# Revit family: Specialty_Equipment-Fiberglass_Planter-Planters_Unlimited-Tuscana Rectangular & Square
name_source: partatom
category: Specialty Equipment
units: mm (PartAtom-declared; Revit-internal decimal feet)

## family parameters
Always vertical = Yes
Cut with Voids When Loaded = No
Enable Cutting in Views = No
Maintain Annotation Orientation = No
OmniClass Number = 23.40.05.21.17
OmniClass Title = Planters
Part Type = Normal
Room Calculation Point = No
Round Connector Dimension = Use Diameter
Shared = No
Work Plane-Based = No

## types (420) — shared parameters
Assembly Code = G2050600
CD_Divider Thickness = 0.4"
CD_Finish = Plastic-Fiberglass-Carlsbad-Semi_Gloss-Charcoal
CD_Microsite = https://www.caddetails.com
CD_OD = 0.4"
CD_Pad Size = 3.0"
CD_Pad Spacing = 5.0"
CD_Product Page URL = https://www.plantersunlimited.com
CD_Specification = https://www.plantersunlimited.com
Default Elevation = 0.0"
Manufacturer = Planters Unlimited
Model = Tuscana Series Planter
URL = https://www.plantersunlimited.com

## per-type parameters (varying)
| type | CD_Divider | CD_Height | CD_Length | CD_Width | Description | Type Comments |
| 30"L x 18"W x 18"H | No | 18.0" | 30.0" | 18.0" | Tuscana Rectangular Planter | Rectangular Planter |
| 30"L x 18"W x 24"H | No | 24.0" | 30.0" | 18.0" | Tuscana Rectangular Planter | Rectangular Planter |
| 30"L x 18"W x 30"H | No | 30.0" | 30.0" | 18.0" | Tuscana Rectangular Planter | Rectangular Planter |
| 30"L x 18"W x 36"H | No | 36.0" | 30.0" | 18.0" | Tuscana Rectangular Planter | Rectangular Planter |
| 30"L x 18"W x 42"H | No | 42.0" | 30.0" | 18.0" | Tuscana Rectangular Planter | Rectangular Planter |
| 30"L x 18"W x 48"H | No | 48.0" | 30.0" | 18.0" | Tuscana Rectangular Planter | Rectangular Planter |
| 30"L x 24"W x 18"H | No | 18.0" | 30.0" | 24.0" | Tuscana Rectangular Planter | Rectangular Planter |
| 30"L x 24"W x 24"H | No | 24.0" | 30.0" | 24.0" | Tuscana Rectangular Planter | Rectangular Planter |
| 30"L x 24"W x 30"H | No | 30.0" | 30.0" | 24.0" | Tuscana Rectangular Planter | Rectangular Planter |
| 30"L x 24"W x 36"H | No | 36.0" | 30.0" | 24.0" | Tuscana Rectangular Planter | Rectangular Planter |
| 30"L x 24"W x 42"H | No | 42.0" | 30.0" | 24.0" | Tuscana Rectangular Planter | Rectangular Planter |
| 30"L x 24"W x 48"H | No | 48.0" | 30.0" | 24.0" | Tuscana Rectangular Planter | Rectangular Planter |
| 30"L x 30"W x 18"H | No | 18.0" | 30.0" | 30.0" | Tuscana Square Planter | Square Planter |
| 30"L x 30"W x 24"H | No | 24.0" | 30.0" | 30.0" | Tuscana Square Planter | Square Planter |
| 30"L x 30"W x 30"H | No | 30.0" | 30.0" | 30.0" | Tuscana Square Planter | Square Planter |
| 30"L x 30"W x 36"H | No | 36.0" | 30.0" | 30.0" | Tuscana Square Planter | Square Planter |
| 30"L x 30"W x 42"H | No | 42.0" | 30.0" | 30.0" | Tuscana Square Planter | Square Planter |
| 30"L x 30"W x 48"H | No | 48.0" | 30.0" | 30.0" | Tuscana Square Planter | Square Planter |
| 30"L x 36"W x 18"H | No | 18.0" | 30.0" | 36.0" | Tuscana Rectangular Planter | Rectangular Planter |
| 30"L x 36"W x 24"H | No | 24.0" | 30.0" | 36.0" | Tuscana Rectangular Planter | Rectangular Planter |
| 30"L x 36"W x 30"H | No | 30.0" | 30.0" | 36.0" | Tuscana Rectangular Planter | Rectangular Planter |
| 30"L x 36"W x 36"H | No | 36.0" | 30.0" | 36.0" | Tuscana Rectangular Planter | Rectangular Planter |
| 30"L x 36"W x 42"H | No | 42.0" | 30.0" | 36.0" | Tuscana Rectangular Planter | Rectangular Planter |
| 30"L x 36"W x 48"H | No | 48.0" | 30.0" | 36.0" | Tuscana Rectangular Planter | Rectangular Planter |
| 30"L x 42"W x 18"H | No | 18.0" | 30.0" | 42.0" | Tuscana Rectangular Planter | Rectangular Planter |
| 30"L x 42"W x 24"H | No | 24.0" | 30.0" | 42.0" | Tuscana Rectangular Planter | Rectangular Planter |
| 30"L x 42"W x 30"H | No | 30.0" | 30.0" | 42.0" | Tuscana Rectangular Planter | Rectangular Planter |
| 30"L x 42"W x 36"H | No | 36.0" | 30.0" | 42.0" | Tuscana Rectangular Planter | Rectangular Planter |
| 30"L x 42"W x 42"H | No | 42.0" | 30.0" | 42.0" | Tuscana Rectangular Planter | Rectangular Planter |
| 30"L x 42"W x 48"H | No | 48.0" | 30.0" | 42.0" | Tuscana Rectangular Planter | Rectangular Planter |
| 36"L x 18"W x 18"H | No | 18.0" | 36.0" | 18.0" | Tuscana Rectangular Planter | Rectangular Planter |
| 36"L x 18"W x 24"H | No | 24.0" | 36.0" | 18.0" | Tuscana Rectangular Planter | Rectangular Planter |
| 36"L x 18"W x 30"H | No | 30.0" | 36.0" | 18.0" | Tuscana Rectangular Planter | Rectangular Planter |
| 36"L x 18"W x 36"H | No | 36.0" | 36.0" | 18.0" | Tuscana Rectangular Planter | Rectangular Planter |
| 36"L x 18"W x 42"H | No | 42.0" | 36.0" | 18.0" | Tuscana Rectangular Planter | Rectangular Planter |
| 36"L x 18"W x 48"H | No | 48.0" | 36.0" | 18.0" | Tuscana Rectangular Planter | Rectangular Planter |
| 36"L x 24"W x 18"H | No | 18.0" | 36.0" | 24.0" | Tuscana Rectangular Planter | Rectangular Planter |
| 36"L x 24"W x 24"H | No | 24.0" | 36.0" | 24.0" | Tuscana Rectangular Planter | Rectangular Planter |
| 36"L x 24"W x 30"H | No | 30.0" | 36.0" | 24.0" | Tuscana Rectangular Planter | Rectangular Planter |
| 36"L x 24"W x 36"H | No | 36.0" | 36.0" | 24.0" | Tuscana Rectangular Planter | Rectangular Planter |
| 36"L x 24"W x 42"H | No | 42.0" | 36.0" | 24.0" | Tuscana Rectangular Planter | Rectangular Planter |
| 36"L x 24"W x 48"H | No | 48.0" | 36.0" | 24.0" | Tuscana Rectangular Planter | Rectangular Planter |
| 36"L x 30"W x 18"H | No | 18.0" | 36.0" | 30.0" | Tuscana Rectangular Planter | Rectangular Planter |
| 36"L x 30"W x 24"H | No | 24.0" | 36.0" | 30.0" | Tuscana Rectangular Planter | Rectangular Planter |
| 36"L x 30"W x 30"H | No | 30.0" | 36.0" | 30.0" | Tuscana Rectangular Planter | Rectangular Planter |
| 36"L x 30"W x 36"H | No | 36.0" | 36.0" | 30.0" | Tuscana Rectangular Planter | Rectangular Planter |
| 36"L x 30"W x 42"H | No | 42.0" | 36.0" | 30.0" | Tuscana Rectangular Planter | Rectangular Planter |
| 36"L x 30"W x 48"H | No | 48.0" | 36.0" | 30.0" | Tuscana Rectangular Planter | Rectangular Planter |
| 36"L x 36"W x 18"H | No | 18.0" | 36.0" | 36.0" | Tuscana Square Planter | Square Planter |
| 36"L x 36"W x 24"H | No | 24.0" | 36.0" | 36.0" | Tuscana Square Planter | Square Planter |
| 36"L x 36"W x 30"H | No | 30.0" | 36.0" | 36.0" | Tuscana Square Planter | Square Planter |
| 36"L x 36"W x 36"H | No | 36.0" | 36.0" | 36.0" | Tuscana Square Planter | Square Planter |
| 36"L x 36"W x 42"H | No | 42.0" | 36.0" | 36.0" | Tuscana Square Planter | Square Planter |
| 36"L x 36"W x 48"H | No | 48.0" | 36.0" | 36.0" | Tuscana Square Planter | Square Planter |
| 36"L x 42"W x 18"H | No | 18.0" | 36.0" | 42.0" | Tuscana Rectangular Planter | Rectangular Planter |
| 36"L x 42"W x 24"H | No | 24.0" | 36.0" | 42.0" | Tuscana Rectangular Planter | Rectangular Planter |
| 36"L x 42"W x 30"H | No | 30.0" | 36.0" | 42.0" | Tuscana Rectangular Planter | Rectangular Planter |
| 36"L x 42"W x 36"H | No | 36.0" | 36.0" | 42.0" | Tuscana Rectangular Planter | Rectangular Planter |
| 36"L x 42"W x 42"H | No | 42.0" | 36.0" | 42.0" | Tuscana Rectangular Planter | Rectangular Planter |
| 36"L x 42"W x 48"H | No | 48.0" | 36.0" | 42.0" | Tuscana Rectangular Planter | Rectangular Planter |
| 42"L x 18"W x 18"H | No | 18.0" | 42.0" | 18.0" | Tuscana Rectangular Planter | Rectangular Planter |
| 42"L x 18"W x 24"H | No | 24.0" | 42.0" | 18.0" | Tuscana Rectangular Planter | Rectangular Planter |
| 42"L x 18"W x 30"H | No | 30.0" | 42.0" | 18.0" | Tuscana Rectangular Planter | Rectangular Planter |
| 42"L x 18"W x 36"H | No | 36.0" | 42.0" | 18.0" | Tuscana Rectangular Planter | Rectangular Planter |
| 42"L x 18"W x 42"H | No | 42.0" | 42.0" | 18.0" | Tuscana Rectangular Planter | Rectangular Planter |
| 42"L x 18"W x 48"H | No | 48.0" | 42.0" | 18.0" | Tuscana Rectangular Planter | Rectangular Planter |
| 42"L x 24"W x 18"H | No | 18.0" | 42.0" | 24.0" | Tuscana Rectangular Planter | Rectangular Planter |
| 42"L x 24"W x 24"H | No | 24.0" | 42.0" | 24.0" | Tuscana Rectangular Planter | Rectangular Planter |
| 42"L x 24"W x 30"H | No | 30.0" | 42.0" | 24.0" | Tuscana Rectangular Planter | Rectangular Planter |
| 42"L x 24"W x 36"H | No | 36.0" | 42.0" | 24.0" | Tuscana Rectangular Planter | Rectangular Planter |
| 42"L x 24"W x 42"H | No | 42.0" | 42.0" | 24.0" | Tuscana Rectangular Planter | Rectangular Planter |
| 42"L x 24"W x 48"H | No | 48.0" | 42.0" | 24.0" | Tuscana Rectangular Planter | Rectangular Planter |
| 42"L x 30"W x 18"H | No | 18.0" | 42.0" | 30.0" | Tuscana Rectangular Planter | Rectangular Planter |
| 42"L x 30"W x 24"H | No | 24.0" | 42.0" | 30.0" | Tuscana Rectangular Planter | Rectangular Planter |
| 42"L x 30"W x 30"H | No | 30.0" | 42.0" | 30.0" | Tuscana Rectangular Planter | Rectangular Planter |
| 42"L x 30"W x 36"H | No | 36.0" | 42.0" | 30.0" | Tuscana Rectangular Planter | Rectangular Planter |
| 42"L x 30"W x 42"H | No | 42.0" | 42.0" | 30.0" | Tuscana Rectangular Planter | Rectangular Planter |
| 42"L x 30"W x 48"H | No | 48.0" | 42.0" | 30.0" | Tuscana Rectangular Planter | Rectangular Planter |
| 42"L x 36"W x 18"H | No | 18.0" | 42.0" | 36.0" | Tuscana Rectangular Planter | Rectangular Planter |
| 42"L x 36"W x 24"H | No | 24.0" | 42.0" | 36.0" | Tuscana Rectangular Planter | Rectangular Planter |
| 42"L x 36"W x 30"H | No | 30.0" | 42.0" | 36.0" | Tuscana Rectangular Planter | Rectangular Planter |
| 42"L x 36"W x 36"H | No | 36.0" | 42.0" | 36.0" | Tuscana Rectangular Planter | Rectangular Planter |
| 42"L x 36"W x 42"H | No | 42.0" | 42.0" | 36.0" | Tuscana Rectangular Planter | Rectangular Planter |
| 42"L x 36"W x 48"H | No | 48.0" | 42.0" | 36.0" | Tuscana Rectangular Planter | Rectangular Planter |
| 42"L x 42"W x 18"H | No | 18.0" | 42.0" | 42.0" | Tuscana Square Planter | Square Planter |
| 42"L x 42"W x 24"H | No | 24.0" | 42.0" | 42.0" | Tuscana Square Planter | Square Planter |
| 42"L x 42"W x 30"H | No | 30.0" | 42.0" | 42.0" | Tuscana Square Planter | Square Planter |
| 42"L x 42"W x 36"H | No | 36.0" | 42.0" | 42.0" | Tuscana Square Planter | Square Planter |
| 42"L x 42"W x 42"H | No | 42.0" | 42.0" | 42.0" | Tuscana Square Planter | Square Planter |
| 42"L x 42"W x 48"H | No | 48.0" | 42.0" | 42.0" | Tuscana Square Planter | Square Planter |
| 48"L x 18"W x 18"H | No | 18.0" | 48.0" | 18.0" | Tuscana Rectangular Planter | Rectangular Planter |
| 48"L x 18"W x 24"H | No | 24.0" | 48.0" | 18.0" | Tuscana Rectangular Planter | Rectangular Planter |
| 48"L x 18"W x 30"H | No | 30.0" | 48.0" | 18.0" | Tuscana Rectangular Planter | Rectangular Planter |
| 48"L x 18"W x 36"H | No | 36.0" | 48.0" | 18.0" | Tuscana Rectangular Planter | Rectangular Planter |
| 48"L x 18"W x 42"H | No | 42.0" | 48.0" | 18.0" | Tuscana Rectangular Planter | Rectangular Planter |
| 48"L x 18"W x 48"H | No | 48.0" | 48.0" | 18.0" | Tuscana Rectangular Planter | Rectangular Planter |
| 48"L x 24"W x 18"H | No | 18.0" | 48.0" | 24.0" | Tuscana Rectangular Planter | Rectangular Planter |
| 48"L x 24"W x 24"H | No | 24.0" | 48.0" | 24.0" | Tuscana Rectangular Planter | Rectangular Planter |
| 48"L x 24"W x 30"H | No | 30.0" | 48.0" | 24.0" | Tuscana Rectangular Planter | Rectangular Planter |
| 48"L x 24"W x 36"H | No | 36.0" | 48.0" | 24.0" | Tuscana Rectangular Planter | Rectangular Planter |
| 48"L x 24"W x 42"H | No | 42.0" | 48.0" | 24.0" | Tuscana Rectangular Planter | Rectangular Planter |
| 48"L x 24"W x 48"H | No | 48.0" | 48.0" | 24.0" | Tuscana Rectangular Planter | Rectangular Planter |
| 48"L x 30"W x 18"H | No | 18.0" | 48.0" | 30.0" | Tuscana Rectangular Planter | Rectangular Planter |
| 48"L x 30"W x 24"H | No | 24.0" | 48.0" | 30.0" | Tuscana Rectangular Planter | Rectangular Planter |
| 48"L x 30"W x 30"H | No | 30.0" | 48.0" | 30.0" | Tuscana Rectangular Planter | Rectangular Planter |
| 48"L x 30"W x 36"H | No | 36.0" | 48.0" | 30.0" | Tuscana Rectangular Planter | Rectangular Planter |
| 48"L x 30"W x 42"H | No | 42.0" | 48.0" | 30.0" | Tuscana Rectangular Planter | Rectangular Planter |
| 48"L x 30"W x 48"H | No | 48.0" | 48.0" | 30.0" | Tuscana Rectangular Planter | Rectangular Planter |
| 48"L x 36"W x 18"H | No | 18.0" | 48.0" | 36.0" | Tuscana Rectangular Planter | Rectangular Planter |
| 48"L x 36"W x 24"H | No | 24.0" | 48.0" | 36.0" | Tuscana Rectangular Planter | Rectangular Planter |
| 48"L x 36"W x 30"H | No | 30.0" | 48.0" | 36.0" | Tuscana Rectangular Planter | Rectangular Planter |
| 48"L x 36"W x 36"H | No | 36.0" | 48.0" | 36.0" | Tuscana Rectangular Planter | Rectangular Planter |
| 48"L x 36"W x 42"H | No | 42.0" | 48.0" | 36.0" | Tuscana Rectangular Planter | Rectangular Planter |
| 48"L x 36"W x 48"H | No | 48.0" | 48.0" | 36.0" | Tuscana Rectangular Planter | Rectangular Planter |
| 48"L x 42"W x 18"H | No | 18.0" | 48.0" | 42.0" | Tuscana Rectangular Planter | Rectangular Planter |
| 48"L x 42"W x 24"H | No | 24.0" | 48.0" | 42.0" | Tuscana Rectangular Planter | Rectangular Planter |
| 48"L x 42"W x 30"H | No | 30.0" | 48.0" | 42.0" | Tuscana Rectangular Planter | Rectangular Planter |
| 48"L x 42"W x 36"H | No | 36.0" | 48.0" | 42.0" | Tuscana Rectangular Planter | Rectangular Planter |
| 48"L x 42"W x 42"H | No | 42.0" | 48.0" | 42.0" | Tuscana Rectangular Planter | Rectangular Planter |
| 48"L x 42"W x 48"H | No | 48.0" | 48.0" | 42.0" | Tuscana Rectangular Planter | Rectangular Planter |
| 54"L x 18"W x 18"H | Yes | 18.0" | 54.0" | 18.0" | Tuscana Rectangular Planter | Rectangular Planter |
| 54"L x 18"W x 24"H | Yes | 24.0" | 54.0" | 18.0" | Tuscana Rectangular Planter | Rectangular Planter |
| 54"L x 18"W x 30"H | Yes | 30.0" | 54.0" | 18.0" | Tuscana Rectangular Planter | Rectangular Planter |
| 54"L x 18"W x 36"H | Yes | 36.0" | 54.0" | 18.0" | Tuscana Rectangular Planter | Rectangular Planter |
| 54"L x 18"W x 42"H | Yes | 42.0" | 54.0" | 18.0" | Tuscana Rectangular Planter | Rectangular Planter |
| 54"L x 18"W x 48"H | Yes | 48.0" | 54.0" | 18.0" | Tuscana Rectangular Planter | Rectangular Planter |
| 54"L x 24"W x 18"H | Yes | 18.0" | 54.0" | 24.0" | Tuscana Rectangular Planter | Rectangular Planter |
| 54"L x 24"W x 24"H | Yes | 24.0" | 54.0" | 24.0" | Tuscana Rectangular Planter | Rectangular Planter |
| 54"L x 24"W x 30"H | Yes | 30.0" | 54.0" | 24.0" | Tuscana Rectangular Planter | Rectangular Planter |
| 54"L x 24"W x 36"H | Yes | 36.0" | 54.0" | 24.0" | Tuscana Rectangular Planter | Rectangular Planter |
| 54"L x 24"W x 42"H | Yes | 42.0" | 54.0" | 24.0" | Tuscana Rectangular Planter | Rectangular Planter |
| 54"L x 24"W x 48"H | Yes | 48.0" | 54.0" | 24.0" | Tuscana Rectangular Planter | Rectangular Planter |
| 54"L x 30"W x 18"H | Yes | 18.0" | 54.0" | 30.0" | Tuscana Rectangular Planter | Rectangular Planter |
| 54"L x 30"W x 24"H | Yes | 24.0" | 54.0" | 30.0" | Tuscana Rectangular Planter | Rectangular Planter |
| 54"L x 30"W x 30"H | Yes | 30.0" | 54.0" | 30.0" | Tuscana Rectangular Planter | Rectangular Planter |
| 54"L x 30"W x 36"H | Yes | 36.0" | 54.0" | 30.0" | Tuscana Rectangular Planter | Rectangular Planter |
| 54"L x 30"W x 42"H | Yes | 42.0" | 54.0" | 30.0" | Tuscana Rectangular Planter | Rectangular Planter |
| 54"L x 30"W x 48"H | Yes | 48.0" | 54.0" | 30.0" | Tuscana Rectangular Planter | Rectangular Planter |
| 54"L x 36"W x 18"H | Yes | 18.0" | 54.0" | 36.0" | Tuscana Rectangular Planter | Rectangular Planter |
| 54"L x 36"W x 24"H | Yes | 24.0" | 54.0" | 36.0" | Tuscana Rectangular Planter | Rectangular Planter |
| 54"L x 36"W x 30"H | Yes | 30.0" | 54.0" | 36.0" | Tuscana Rectangular Planter | Rectangular Planter |
| 54"L x 36"W x 36"H | Yes | 36.0" | 54.0" | 36.0" | Tuscana Rectangular Planter | Rectangular Planter |
| 54"L x 36"W x 42"H | Yes | 42.0" | 54.0" | 36.0" | Tuscana Rectangular Planter | Rectangular Planter |
| 54"L x 36"W x 48"H | Yes | 48.0" | 54.0" | 36.0" | Tuscana Rectangular Planter | Rectangular Planter |
| 54"L x 42"W x 18"H | Yes | 18.0" | 54.0" | 42.0" | Tuscana Rectangular Planter | Rectangular Planter |
| 54"L x 42"W x 24"H | Yes | 24.0" | 54.0" | 42.0" | Tuscana Rectangular Planter | Rectangular Planter |
| 54"L x 42"W x 30"H | Yes | 30.0" | 54.0" | 42.0" | Tuscana Rectangular Planter | Rectangular Planter |
| 54"L x 42"W x 36"H | Yes | 36.0" | 54.0" | 42.0" | Tuscana Rectangular Planter | Rectangular Planter |
| 54"L x 42"W x 42"H | Yes | 42.0" | 54.0" | 42.0" | Tuscana Rectangular Planter | Rectangular Planter |
| 54"L x 42"W x 48"H | Yes | 48.0" | 54.0" | 42.0" | Tuscana Rectangular Planter | Rectangular Planter |
| 60"L x 18"W x 18"H | Yes | 18.0" | 60.0" | 18.0" | Tuscana Rectangular Planter | Rectangular Planter |
| 60"L x 18"W x 24"H | Yes | 24.0" | 60.0" | 18.0" | Tuscana Rectangular Planter | Rectangular Planter |
| 60"L x 18"W x 30"H | Yes | 30.0" | 60.0" | 18.0" | Tuscana Rectangular Planter | Rectangular Planter |
| 60"L x 18"W x 36"H | Yes | 36.0" | 60.0" | 18.0" | Tuscana Rectangular Planter | Rectangular Planter |
| 60"L x 18"W x 42"H | Yes | 42.0" | 60.0" | 18.0" | Tuscana Rectangular Planter | Rectangular Planter |
| 60"L x 18"W x 48"H | Yes | 48.0" | 60.0" | 18.0" | Tuscana Rectangular Planter | Rectangular Planter |
| 60"L x 24"W x 18"H | Yes | 18.0" | 60.0" | 24.0" | Tuscana Rectangular Planter | Rectangular Planter |
| 60"L x 24"W x 24"H | Yes | 24.0" | 60.0" | 24.0" | Tuscana Rectangular Planter | Rectangular Planter |
| 60"L x 24"W x 30"H | Yes | 30.0" | 60.0" | 24.0" | Tuscana Rectangular Planter | Rectangular Planter |
| 60"L x 24"W x 36"H | Yes | 36.0" | 60.0" | 24.0" | Tuscana Rectangular Planter | Rectangular Planter |
| 60"L x 24"W x 42"H | Yes | 42.0" | 60.0" | 24.0" | Tuscana Rectangular Planter | Rectangular Planter |
| 60"L x 24"W x 48"H | Yes | 48.0" | 60.0" | 24.0" | Tuscana Rectangular Planter | Rectangular Planter |
| 60"L x 30"W x 18"H | Yes | 18.0" | 60.0" | 30.0" | Tuscana Rectangular Planter | Rectangular Planter |
| 60"L x 30"W x 24"H | Yes | 24.0" | 60.0" | 30.0" | Tuscana Rectangular Planter | Rectangular Planter |
| 60"L x 30"W x 30"H | Yes | 30.0" | 60.0" | 30.0" | Tuscana Rectangular Planter | Rectangular Planter |
| 60"L x 30"W x 36"H | Yes | 36.0" | 60.0" | 30.0" | Tuscana Rectangular Planter | Rectangular Planter |
| 60"L x 30"W x 42"H | Yes | 42.0" | 60.0" | 30.0" | Tuscana Rectangular Planter | Rectangular Planter |
| 60"L x 30"W x 48"H | Yes | 48.0" | 60.0" | 30.0" | Tuscana Rectangular Planter | Rectangular Planter |
| 60"L x 36"W x 18"H | Yes | 18.0" | 60.0" | 36.0" | Tuscana Rectangular Planter | Rectangular Planter |
| 60"L x 36"W x 24"H | Yes | 24.0" | 60.0" | 36.0" | Tuscana Rectangular Planter | Rectangular Planter |
| 60"L x 36"W x 30"H | Yes | 30.0" | 60.0" | 36.0" | Tuscana Rectangular Planter | Rectangular Planter |
| 60"L x 36"W x 36"H | Yes | 36.0" | 60.0" | 36.0" | Tuscana Rectangular Planter | Rectangular Planter |
| 60"L x 36"W x 42"H | Yes | 42.0" | 60.0" | 36.0" | Tuscana Rectangular Planter | Rectangular Planter |
| 60"L x 36"W x 48"H | Yes | 48.0" | 60.0" | 36.0" | Tuscana Rectangular Planter | Rectangular Planter |
| 60"L x 42"W x 18"H | Yes | 18.0" | 60.0" | 42.0" | Tuscana Rectangular Planter | Rectangular Planter |
| 60"L x 42"W x 24"H | Yes | 24.0" | 60.0" | 42.0" | Tuscana Rectangular Planter | Rectangular Planter |
| 60"L x 42"W x 30"H | Yes | 30.0" | 60.0" | 42.0" | Tuscana Rectangular Planter | Rectangular Planter |
| 60"L x 42"W x 36"H | Yes | 36.0" | 60.0" | 42.0" | Tuscana Rectangular Planter | Rectangular Planter |
| 60"L x 42"W x 42"H | Yes | 42.0" | 60.0" | 42.0" | Tuscana Rectangular Planter | Rectangular Planter |
| 60"L x 42"W x 48"H | Yes | 48.0" | 60.0" | 42.0" | Tuscana Rectangular Planter | Rectangular Planter |
| 66"L x 18"W x 18"H | Yes | 18.0" | 66.0" | 18.0" | Tuscana Rectangular Planter | Rectangular Planter |
| 66"L x 18"W x 24"H | Yes | 24.0" | 66.0" | 18.0" | Tuscana Rectangular Planter | Rectangular Planter |
| 66"L x 18"W x 30"H | Yes | 30.0" | 66.0" | 18.0" | Tuscana Rectangular Planter | Rectangular Planter |
| 66"L x 18"W x 36"H | Yes | 36.0" | 66.0" | 18.0" | Tuscana Rectangular Planter | Rectangular Planter |
| 66"L x 18"W x 42"H | Yes | 42.0" | 66.0" | 18.0" | Tuscana Rectangular Planter | Rectangular Planter |
| 66"L x 18"W x 48"H | Yes | 48.0" | 66.0" | 18.0" | Tuscana Rectangular Planter | Rectangular Planter |
| 66"L x 24"W x 18"H | Yes | 18.0" | 66.0" | 24.0" | Tuscana Rectangular Planter | Rectangular Planter |
| 66"L x 24"W x 24"H | Yes | 24.0" | 66.0" | 24.0" | Tuscana Rectangular Planter | Rectangular Planter |
| 66"L x 24"W x 30"H | Yes | 30.0" | 66.0" | 24.0" | Tuscana Rectangular Planter | Rectangular Planter |
| 66"L x 24"W x 36"H | Yes | 36.0" | 66.0" | 24.0" | Tuscana Rectangular Planter | Rectangular Planter |
| 66"L x 24"W x 42"H | Yes | 42.0" | 66.0" | 24.0" | Tuscana Rectangular Planter | Rectangular Planter |
| 66"L x 24"W x 48"H | Yes | 48.0" | 66.0" | 24.0" | Tuscana Rectangular Planter | Rectangular Planter |
| 66"L x 30"W x 18"H | Yes | 18.0" | 66.0" | 30.0" | Tuscana Rectangular Planter | Rectangular Planter |
| 66"L x 30"W x 24"H | Yes | 24.0" | 66.0" | 30.0" | Tuscana Rectangular Planter | Rectangular Planter |
| 66"L x 30"W x 30"H | Yes | 30.0" | 66.0" | 30.0" | Tuscana Rectangular Planter | Rectangular Planter |
| 66"L x 30"W x 36"H | Yes | 36.0" | 66.0" | 30.0" | Tuscana Rectangular Planter | Rectangular Planter |
| 66"L x 30"W x 42"H | Yes | 42.0" | 66.0" | 30.0" | Tuscana Rectangular Planter | Rectangular Planter |
| 66"L x 30"W x 48"H | Yes | 48.0" | 66.0" | 30.0" | Tuscana Rectangular Planter | Rectangular Planter |
| 66"L x 36"W x 18"H | Yes | 18.0" | 66.0" | 36.0" | Tuscana Rectangular Planter | Rectangular Planter |
| 66"L x 36"W x 24"H | Yes | 24.0" | 66.0" | 36.0" | Tuscana Rectangular Planter | Rectangular Planter |
| 66"L x 36"W x 30"H | Yes | 30.0" | 66.0" | 36.0" | Tuscana Rectangular Planter | Rectangular Planter |
| 66"L x 36"W x 36"H | Yes | 36.0" | 66.0" | 36.0" | Tuscana Rectangular Planter | Rectangular Planter |
| 66"L x 36"W x 42"H | Yes | 42.0" | 66.0" | 36.0" | Tuscana Rectangular Planter | Rectangular Planter |
| 66"L x 36"W x 48"H | Yes | 48.0" | 66.0" | 36.0" | Tuscana Rectangular Planter | Rectangular Planter |
| 66"L x 42"W x 18"H | Yes | 18.0" | 66.0" | 42.0" | Tuscana Rectangular Planter | Rectangular Planter |
| 66"L x 42"W x 24"H | Yes | 24.0" | 66.0" | 42.0" | Tuscana Rectangular Planter | Rectangular Planter |
| 66"L x 42"W x 30"H | Yes | 30.0" | 66.0" | 42.0" | Tuscana Rectangular Planter | Rectangular Planter |
| 66"L x 42"W x 36"H | Yes | 36.0" | 66.0" | 42.0" | Tuscana Rectangular Planter | Rectangular Planter |
| 66"L x 42"W x 42"H | Yes | 42.0" | 66.0" | 42.0" | Tuscana Rectangular Planter | Rectangular Planter |
| 66"L x 42"W x 48"H | Yes | 48.0" | 66.0" | 42.0" | Tuscana Rectangular Planter | Rectangular Planter |
| 72"L x 18"W x 18"H | Yes | 18.0" | 72.0" | 18.0" | Tuscana Rectangular Planter | Rectangular Planter |
| 72"L x 18"W x 24"H | Yes | 24.0" | 72.0" | 18.0" | Tuscana Rectangular Planter | Rectangular Planter |
| 72"L x 18"W x 30"H | Yes | 30.0" | 72.0" | 18.0" | Tuscana Rectangular Planter | Rectangular Planter |
| 72"L x 18"W x 36"H | Yes | 36.0" | 72.0" | 18.0" | Tuscana Rectangular Planter | Rectangular Planter |
| 72"L x 18"W x 42"H | Yes | 42.0" | 72.0" | 18.0" | Tuscana Rectangular Planter | Rectangular Planter |
| 72"L x 18"W x 48"H | Yes | 48.0" | 72.0" | 18.0" | Tuscana Rectangular Planter | Rectangular Planter |
| 72"L x 24"W x 18"H | Yes | 18.0" | 72.0" | 24.0" | Tuscana Rectangular Planter | Rectangular Planter |
| 72"L x 24"W x 24"H | Yes | 24.0" | 72.0" | 24.0" | Tuscana Rectangular Planter | Rectangular Planter |
| 72"L x 24"W x 30"H | Yes | 30.0" | 72.0" | 24.0" | Tuscana Rectangular Planter | Rectangular Planter |
| 72"L x 24"W x 36"H | Yes | 36.0" | 72.0" | 24.0" | Tuscana Rectangular Planter | Rectangular Planter |
| 72"L x 24"W x 42"H | Yes | 42.0" | 72.0" | 24.0" | Tuscana Rectangular Planter | Rectangular Planter |
| 72"L x 24"W x 48"H | Yes | 48.0" | 72.0" | 24.0" | Tuscana Rectangular Planter | Rectangular Planter |
| 72"L x 30"W x 18"H | Yes | 18.0" | 72.0" | 30.0" | Tuscana Rectangular Planter | Rectangular Planter |
| 72"L x 30"W x 24"H | Yes | 24.0" | 72.0" | 30.0" | Tuscana Rectangular Planter | Rectangular Planter |
| 72"L x 30"W x 30"H | Yes | 30.0" | 72.0" | 30.0" | Tuscana Rectangular Planter | Rectangular Planter |
| 72"L x 30"W x 36"H | Yes | 36.0" | 72.0" | 30.0" | Tuscana Rectangular Planter | Rectangular Planter |
| 72"L x 30"W x 42"H | Yes | 42.0" | 72.0" | 30.0" | Tuscana Rectangular Planter | Rectangular Planter |
| 72"L x 30"W x 48"H | Yes | 48.0" | 72.0" | 30.0" | Tuscana Rectangular Planter | Rectangular Planter |
| 72"L x 36"W x 18"H | Yes | 18.0" | 72.0" | 36.0" | Tuscana Rectangular Planter | Rectangular Planter |
| 72"L x 36"W x 24"H | Yes | 24.0" | 72.0" | 36.0" | Tuscana Rectangular Planter | Rectangular Planter |
| 72"L x 36"W x 30"H | Yes | 30.0" | 72.0" | 36.0" | Tuscana Rectangular Planter | Rectangular Planter |
| 72"L x 36"W x 36"H | Yes | 36.0" | 72.0" | 36.0" | Tuscana Rectangular Planter | Rectangular Planter |
| 72"L x 36"W x 42"H | Yes | 42.0" | 72.0" | 36.0" | Tuscana Rectangular Planter | Rectangular Planter |
| 72"L x 36"W x 48"H | Yes | 48.0" | 72.0" | 36.0" | Tuscana Rectangular Planter | Rectangular Planter |
| 72"L x 42"W x 18"H | Yes | 18.0" | 72.0" | 42.0" | Tuscana Rectangular Planter | Rectangular Planter |
| 72"L x 42"W x 24"H | Yes | 24.0" | 72.0" | 42.0" | Tuscana Rectangular Planter | Rectangular Planter |
| 72"L x 42"W x 30"H | Yes | 30.0" | 72.0" | 42.0" | Tuscana Rectangular Planter | Rectangular Planter |
| 72"L x 42"W x 36"H | Yes | 36.0" | 72.0" | 42.0" | Tuscana Rectangular Planter | Rectangular Planter |
| 72"L x 42"W x 42"H | Yes | 42.0" | 72.0" | 42.0" | Tuscana Rectangular Planter | Rectangular Planter |
| 72"L x 42"W x 48"H | Yes | 48.0" | 72.0" | 42.0" | Tuscana Rectangular Planter | Rectangular Planter |
| 78"L x 18"W x 18"H | Yes | 18.0" | 78.0" | 18.0" | Tuscana Rectangular Planter | Rectangular Planter |
| 78"L x 18"W x 24"H | Yes | 24.0" | 78.0" | 18.0" | Tuscana Rectangular Planter | Rectangular Planter |
| 78"L x 18"W x 30"H | Yes | 30.0" | 78.0" | 18.0" | Tuscana Rectangular Planter | Rectangular Planter |
| 78"L x 18"W x 36"H | Yes | 36.0" | 78.0" | 18.0" | Tuscana Rectangular Planter | Rectangular Planter |
| 78"L x 18"W x 42"H | Yes | 42.0" | 78.0" | 18.0" | Tuscana Rectangular Planter | Rectangular Planter |
| 78"L x 18"W x 48"H | Yes | 48.0" | 78.0" | 18.0" | Tuscana Rectangular Planter | Rectangular Planter |
| 78"L x 24"W x 18"H | Yes | 18.0" | 78.0" | 24.0" | Tuscana Rectangular Planter | Rectangular Planter |
| 78"L x 24"W x 24"H | Yes | 24.0" | 78.0" | 24.0" | Tuscana Rectangular Planter | Rectangular Planter |
| 78"L x 24"W x 30"H | Yes | 30.0" | 78.0" | 24.0" | Tuscana Rectangular Planter | Rectangular Planter |
| 78"L x 24"W x 36"H | Yes | 36.0" | 78.0" | 24.0" | Tuscana Rectangular Planter | Rectangular Planter |
| 78"L x 24"W x 42"H | Yes | 42.0" | 78.0" | 24.0" | Tuscana Rectangular Planter | Rectangular Planter |
| 78"L x 24"W x 48"H | Yes | 48.0" | 78.0" | 24.0" | Tuscana Rectangular Planter | Rectangular Planter |
| 78"L x 30"W x 18"H | Yes | 18.0" | 78.0" | 30.0" | Tuscana Rectangular Planter | Rectangular Planter |
| 78"L x 30"W x 24"H | Yes | 24.0" | 78.0" | 30.0" | Tuscana Rectangular Planter | Rectangular Planter |
| 78"L x 30"W x 30"H | Yes | 30.0" | 78.0" | 30.0" | Tuscana Rectangular Planter | Rectangular Planter |
| 78"L x 30"W x 36"H | Yes | 36.0" | 78.0" | 30.0" | Tuscana Rectangular Planter | Rectangular Planter |
| 78"L x 30"W x 42"H | Yes | 42.0" | 78.0" | 30.0" | Tuscana Rectangular Planter | Rectangular Planter |
| 78"L x 30"W x 48"H | Yes | 48.0" | 78.0" | 30.0" | Tuscana Rectangular Planter | Rectangular Planter |
| 78"L x 36"W x 18"H | Yes | 18.0" | 78.0" | 36.0" | Tuscana Rectangular Planter | Rectangular Planter |
| 78"L x 36"W x 24"H | Yes | 24.0" | 78.0" | 36.0" | Tuscana Rectangular Planter | Rectangular Planter |
| 78"L x 36"W x 30"H | Yes | 30.0" | 78.0" | 36.0" | Tuscana Rectangular Planter | Rectangular Planter |
| 78"L x 36"W x 36"H | Yes | 36.0" | 78.0" | 36.0" | Tuscana Rectangular Planter | Rectangular Planter |
| 78"L x 36"W x 42"H | Yes | 42.0" | 78.0" | 36.0" | Tuscana Rectangular Planter | Rectangular Planter |
| 78"L x 36"W x 48"H | Yes | 48.0" | 78.0" | 36.0" | Tuscana Rectangular Planter | Rectangular Planter |
| 78"L x 42"W x 18"H | Yes | 18.0" | 78.0" | 42.0" | Tuscana Rectangular Planter | Rectangular Planter |
| 78"L x 42"W x 24"H | Yes | 24.0" | 78.0" | 42.0" | Tuscana Rectangular Planter | Rectangular Planter |
| 78"L x 42"W x 30"H | Yes | 30.0" | 78.0" | 42.0" | Tuscana Rectangular Planter | Rectangular Planter |
| 78"L x 42"W x 36"H | Yes | 36.0" | 78.0" | 42.0" | Tuscana Rectangular Planter | Rectangular Planter |
| 78"L x 42"W x 42"H | Yes | 42.0" | 78.0" | 42.0" | Tuscana Rectangular Planter | Rectangular Planter |
| 78"L x 42"W x 48"H | Yes | 48.0" | 78.0" | 42.0" | Tuscana Rectangular Planter | Rectangular Planter |
| 84"L x 18"W x 18"H | Yes | 18.0" | 84.0" | 18.0" | Tuscana Rectangular Planter | Rectangular Planter |
| 84"L x 18"W x 24"H | Yes | 24.0" | 84.0" | 18.0" | Tuscana Rectangular Planter | Rectangular Planter |
| 84"L x 18"W x 30"H | Yes | 30.0" | 84.0" | 18.0" | Tuscana Rectangular Planter | Rectangular Planter |
| 84"L x 18"W x 36"H | Yes | 36.0" | 84.0" | 18.0" | Tuscana Rectangular Planter | Rectangular Planter |
| 84"L x 18"W x 42"H | Yes | 42.0" | 84.0" | 18.0" | Tuscana Rectangular Planter | Rectangular Planter |
| 84"L x 18"W x 48"H | Yes | 48.0" | 84.0" | 18.0" | Tuscana Rectangular Planter | Rectangular Planter |
| 84"L x 24"W x 18"H | Yes | 18.0" | 84.0" | 24.0" | Tuscana Rectangular Planter | Rectangular Planter |
| 84"L x 24"W x 24"H | Yes | 24.0" | 84.0" | 24.0" | Tuscana Rectangular Planter | Rectangular Planter |
| 84"L x 24"W x 30"H | Yes | 30.0" | 84.0" | 24.0" | Tuscana Rectangular Planter | Rectangular Planter |
| 84"L x 24"W x 36"H | Yes | 36.0" | 84.0" | 24.0" | Tuscana Rectangular Planter | Rectangular Planter |
| 84"L x 24"W x 42"H | Yes | 42.0" | 84.0" | 24.0" | Tuscana Rectangular Planter | Rectangular Planter |
| 84"L x 24"W x 48"H | Yes | 48.0" | 84.0" | 24.0" | Tuscana Rectangular Planter | Rectangular Planter |
| 84"L x 30"W x 18"H | Yes | 18.0" | 84.0" | 30.0" | Tuscana Rectangular Planter | Rectangular Planter |
| 84"L x 30"W x 24"H | Yes | 24.0" | 84.0" | 30.0" | Tuscana Rectangular Planter | Rectangular Planter |
| 84"L x 30"W x 30"H | Yes | 30.0" | 84.0" | 30.0" | Tuscana Rectangular Planter | Rectangular Planter |
| 84"L x 30"W x 36"H | Yes | 36.0" | 84.0" | 30.0" | Tuscana Rectangular Planter | Rectangular Planter |
| 84"L x 30"W x 42"H | Yes | 42.0" | 84.0" | 30.0" | Tuscana Rectangular Planter | Rectangular Planter |
| 84"L x 30"W x 48"H | Yes | 48.0" | 84.0" | 30.0" | Tuscana Rectangular Planter | Rectangular Planter |
| 84"L x 36"W x 18"H | Yes | 18.0" | 84.0" | 36.0" | Tuscana Rectangular Planter | Rectangular Planter |
| 84"L x 36"W x 24"H | Yes | 24.0" | 84.0" | 36.0" | Tuscana Rectangular Planter | Rectangular Planter |
| 84"L x 36"W x 30"H | Yes | 30.0" | 84.0" | 36.0" | Tuscana Rectangular Planter | Rectangular Planter |
| 84"L x 36"W x 36"H | Yes | 36.0" | 84.0" | 36.0" | Tuscana Rectangular Planter | Rectangular Planter |
| 84"L x 36"W x 42"H | Yes | 42.0" | 84.0" | 36.0" | Tuscana Rectangular Planter | Rectangular Planter |
| 84"L x 36"W x 48"H | Yes | 48.0" | 84.0" | 36.0" | Tuscana Rectangular Planter | Rectangular Planter |
| 84"L x 42"W x 18"H | Yes | 18.0" | 84.0" | 42.0" | Tuscana Rectangular Planter | Rectangular Planter |
| 84"L x 42"W x 24"H | Yes | 24.0" | 84.0" | 42.0" | Tuscana Rectangular Planter | Rectangular Planter |
| 84"L x 42"W x 30"H | Yes | 30.0" | 84.0" | 42.0" | Tuscana Rectangular Planter | Rectangular Planter |
| 84"L x 42"W x 36"H | Yes | 36.0" | 84.0" | 42.0" | Tuscana Rectangular Planter | Rectangular Planter |
| 84"L x 42"W x 42"H | Yes | 42.0" | 84.0" | 42.0" | Tuscana Rectangular Planter | Rectangular Planter |
| 84"L x 42"W x 48"H | Yes | 48.0" | 84.0" | 42.0" | Tuscana Rectangular Planter | Rectangular Planter |
| 90"L x 18"W x 18"H | Yes | 18.0" | 90.0" | 18.0" | Tuscana Rectangular Planter | Rectangular Planter |
| 90"L x 18"W x 24"H | Yes | 24.0" | 90.0" | 18.0" | Tuscana Rectangular Planter | Rectangular Planter |
| 90"L x 18"W x 30"H | Yes | 30.0" | 90.0" | 18.0" | Tuscana Rectangular Planter | Rectangular Planter |
| 90"L x 18"W x 36"H | Yes | 36.0" | 90.0" | 18.0" | Tuscana Rectangular Planter | Rectangular Planter |
| 90"L x 18"W x 42"H | Yes | 42.0" | 90.0" | 18.0" | Tuscana Rectangular Planter | Rectangular Planter |
| 90"L x 18"W x 48"H | Yes | 48.0" | 90.0" | 18.0" | Tuscana Rectangular Planter | Rectangular Planter |
| 90"L x 24"W x 18"H | Yes | 18.0" | 90.0" | 24.0" | Tuscana Rectangular Planter | Rectangular Planter |
| 90"L x 24"W x 24"H | Yes | 24.0" | 90.0" | 24.0" | Tuscana Rectangular Planter | Rectangular Planter |
| 90"L x 24"W x 30"H | Yes | 30.0" | 90.0" | 24.0" | Tuscana Rectangular Planter | Rectangular Planter |
| 90"L x 24"W x 36"H | Yes | 36.0" | 90.0" | 24.0" | Tuscana Rectangular Planter | Rectangular Planter |
| 90"L x 24"W x 42"H | Yes | 42.0" | 90.0" | 24.0" | Tuscana Rectangular Planter | Rectangular Planter |
| 90"L x 24"W x 48"H | Yes | 48.0" | 90.0" | 24.0" | Tuscana Rectangular Planter | Rectangular Planter |
| 90"L x 30"W x 18"H | Yes | 18.0" | 90.0" | 30.0" | Tuscana Rectangular Planter | Rectangular Planter |
| 90"L x 30"W x 24"H | Yes | 24.0" | 90.0" | 30.0" | Tuscana Rectangular Planter | Rectangular Planter |
| 90"L x 30"W x 30"H | Yes | 30.0" | 90.0" | 30.0" | Tuscana Rectangular Planter | Rectangular Planter |
| 90"L x 30"W x 36"H | Yes | 36.0" | 90.0" | 30.0" | Tuscana Rectangular Planter | Rectangular Planter |
| 90"L x 30"W x 42"H | Yes | 42.0" | 90.0" | 30.0" | Tuscana Rectangular Planter | Rectangular Planter |
| 90"L x 30"W x 48"H | Yes | 48.0" | 90.0" | 30.0" | Tuscana Rectangular Planter | Rectangular Planter |
| 90"L x 36"W x 18"H | Yes | 18.0" | 90.0" | 36.0" | Tuscana Rectangular Planter | Rectangular Planter |
| 90"L x 36"W x 24"H | Yes | 24.0" | 90.0" | 36.0" | Tuscana Rectangular Planter | Rectangular Planter |
| 90"L x 36"W x 30"H | Yes | 30.0" | 90.0" | 36.0" | Tuscana Rectangular Planter | Rectangular Planter |
| 90"L x 36"W x 36"H | Yes | 36.0" | 90.0" | 36.0" | Tuscana Rectangular Planter | Rectangular Planter |
| 90"L x 36"W x 42"H | Yes | 42.0" | 90.0" | 36.0" | Tuscana Rectangular Planter | Rectangular Planter |
| 90"L x 36"W x 48"H | Yes | 48.0" | 90.0" | 36.0" | Tuscana Rectangular Planter | Rectangular Planter |
| 90"L x 42"W x 18"H | Yes | 18.0" | 90.0" | 42.0" | Tuscana Rectangular Planter | Rectangular Planter |
| 90"L x 42"W x 24"H | Yes | 24.0" | 90.0" | 42.0" | Tuscana Rectangular Planter | Rectangular Planter |
| 90"L x 42"W x 30"H | Yes | 30.0" | 90.0" | 42.0" | Tuscana Rectangular Planter | Rectangular Planter |
| 90"L x 42"W x 36"H | Yes | 36.0" | 90.0" | 42.0" | Tuscana Rectangular Planter | Rectangular Planter |
| 90"L x 42"W x 42"H | Yes | 42.0" | 90.0" | 42.0" | Tuscana Rectangular Planter | Rectangular Planter |
| 90"L x 42"W x 48"H | Yes | 48.0" | 90.0" | 42.0" | Tuscana Rectangular Planter | Rectangular Planter |
| 96"L x 18"W x 18"H | Yes | 18.0" | 96.0" | 18.0" | Tuscana Rectangular Planter | Rectangular Planter |
| 96"L x 18"W x 24"H | Yes | 24.0" | 96.0" | 18.0" | Tuscana Rectangular Planter | Rectangular Planter |
| 96"L x 18"W x 30"H | Yes | 30.0" | 96.0" | 18.0" | Tuscana Rectangular Planter | Rectangular Planter |
| 96"L x 18"W x 36"H | Yes | 36.0" | 96.0" | 18.0" | Tuscana Rectangular Planter | Rectangular Planter |
| 96"L x 18"W x 42"H | Yes | 42.0" | 96.0" | 18.0" | Tuscana Rectangular Planter | Rectangular Planter |
| 96"L x 18"W x 48"H | Yes | 48.0" | 96.0" | 18.0" | Tuscana Rectangular Planter | Rectangular Planter |
| 96"L x 24"W x 18"H | Yes | 18.0" | 96.0" | 24.0" | Tuscana Rectangular Planter | Rectangular Planter |
| 96"L x 24"W x 24"H | Yes | 24.0" | 96.0" | 24.0" | Tuscana Rectangular Planter | Rectangular Planter |
| 96"L x 24"W x 30"H | Yes | 30.0" | 96.0" | 24.0" | Tuscana Rectangular Planter | Rectangular Planter |
| 96"L x 24"W x 36"H | Yes | 36.0" | 96.0" | 24.0" | Tuscana Rectangular Planter | Rectangular Planter |
| 96"L x 24"W x 42"H | Yes | 42.0" | 96.0" | 24.0" | Tuscana Rectangular Planter | Rectangular Planter |
| 96"L x 24"W x 48"H | Yes | 48.0" | 96.0" | 24.0" | Tuscana Rectangular Planter | Rectangular Planter |
| 96"L x 30"W x 18"H | Yes | 18.0" | 96.0" | 30.0" | Tuscana Rectangular Planter | Rectangular Planter |
| 96"L x 30"W x 24"H | Yes | 24.0" | 96.0" | 30.0" | Tuscana Rectangular Planter | Rectangular Planter |
| 96"L x 30"W x 30"H | Yes | 30.0" | 96.0" | 30.0" | Tuscana Rectangular Planter | Rectangular Planter |
| 96"L x 30"W x 36"H | Yes | 36.0" | 96.0" | 30.0" | Tuscana Rectangular Planter | Rectangular Planter |
| 96"L x 30"W x 42"H | Yes | 42.0" | 96.0" | 30.0" | Tuscana Rectangular Planter | Rectangular Planter |
| 96"L x 30"W x 48"H | Yes | 48.0" | 96.0" | 30.0" | Tuscana Rectangular Planter | Rectangular Planter |
| 96"L x 36"W x 18"H | Yes | 18.0" | 96.0" | 36.0" | Tuscana Rectangular Planter | Rectangular Planter |
| 96"L x 36"W x 24"H | Yes | 24.0" | 96.0" | 36.0" | Tuscana Rectangular Planter | Rectangular Planter |
| 96"L x 36"W x 30"H | Yes | 30.0" | 96.0" | 36.0" | Tuscana Rectangular Planter | Rectangular Planter |
| 96"L x 36"W x 36"H | Yes | 36.0" | 96.0" | 36.0" | Tuscana Rectangular Planter | Rectangular Planter |
| 96"L x 36"W x 42"H | Yes | 42.0" | 96.0" | 36.0" | Tuscana Rectangular Planter | Rectangular Planter |
| 96"L x 36"W x 48"H | Yes | 48.0" | 96.0" | 36.0" | Tuscana Rectangular Planter | Rectangular Planter |
| 96"L x 42"W x 18"H | Yes | 18.0" | 96.0" | 42.0" | Tuscana Rectangular Planter | Rectangular Planter |
| 96"L x 42"W x 24"H | Yes | 24.0" | 96.0" | 42.0" | Tuscana Rectangular Planter | Rectangular Planter |
| 96"L x 42"W x 30"H | Yes | 30.0" | 96.0" | 42.0" | Tuscana Rectangular Planter | Rectangular Planter |
| 96"L x 42"W x 36"H | Yes | 36.0" | 96.0" | 42.0" | Tuscana Rectangular Planter | Rectangular Planter |
| 96"L x 42"W x 42"H | Yes | 42.0" | 96.0" | 42.0" | Tuscana Rectangular Planter | Rectangular Planter |
| 96"L x 42"W x 48"H | Yes | 48.0" | 96.0" | 42.0" | Tuscana Rectangular Planter | Rectangular Planter |
| 108"L x 18"W x 18"H | Yes | 18.0" | 108.0" | 18.0" | Tuscana Rectangular Planter | Rectangular Planter |
| 108"L x 18"W x 24"H | Yes | 24.0" | 108.0" | 18.0" | Tuscana Rectangular Planter | Rectangular Planter |
| 108"L x 18"W x 30"H | Yes | 30.0" | 108.0" | 18.0" | Tuscana Rectangular Planter | Rectangular Planter |
| 108"L x 18"W x 36"H | Yes | 36.0" | 108.0" | 18.0" | Tuscana Rectangular Planter | Rectangular Planter |
| 108"L x 18"W x 42"H | Yes | 42.0" | 108.0" | 18.0" | Tuscana Rectangular Planter | Rectangular Planter |
| 108"L x 18"W x 48"H | Yes | 48.0" | 108.0" | 18.0" | Tuscana Rectangular Planter | Rectangular Planter |
| 108"L x 24"W x 18"H | Yes | 18.0" | 108.0" | 24.0" | Tuscana Rectangular Planter | Rectangular Planter |
| 108"L x 24"W x 24"H | Yes | 24.0" | 108.0" | 24.0" | Tuscana Rectangular Planter | Rectangular Planter |
| 108"L x 24"W x 30"H | Yes | 30.0" | 108.0" | 24.0" | Tuscana Rectangular Planter | Rectangular Planter |
| 108"L x 24"W x 36"H | Yes | 36.0" | 108.0" | 24.0" | Tuscana Rectangular Planter | Rectangular Planter |
| 108"L x 24"W x 42"H | Yes | 42.0" | 108.0" | 24.0" | Tuscana Rectangular Planter | Rectangular Planter |
| 108"L x 24"W x 48"H | Yes | 48.0" | 108.0" | 24.0" | Tuscana Rectangular Planter | Rectangular Planter |
| 108"L x 30"W x 18"H | Yes | 18.0" | 108.0" | 30.0" | Tuscana Rectangular Planter | Rectangular Planter |
| 108"L x 30"W x 24"H | Yes | 24.0" | 108.0" | 30.0" | Tuscana Rectangular Planter | Rectangular Planter |
| 108"L x 30"W x 30"H | Yes | 30.0" | 108.0" | 30.0" | Tuscana Rectangular Planter | Rectangular Planter |
| 108"L x 30"W x 36"H | Yes | 36.0" | 108.0" | 30.0" | Tuscana Rectangular Planter | Rectangular Planter |
| 108"L x 30"W x 42"H | Yes | 42.0" | 108.0" | 30.0" | Tuscana Rectangular Planter | Rectangular Planter |
| 108"L x 30"W x 48"H | Yes | 48.0" | 108.0" | 30.0" | Tuscana Rectangular Planter | Rectangular Planter |
| 108"L x 36"W x 18"H | Yes | 18.0" | 108.0" | 36.0" | Tuscana Rectangular Planter | Rectangular Planter |
| 108"L x 36"W x 24"H | Yes | 24.0" | 108.0" | 36.0" | Tuscana Rectangular Planter | Rectangular Planter |
| 108"L x 36"W x 30"H | Yes | 30.0" | 108.0" | 36.0" | Tuscana Rectangular Planter | Rectangular Planter |
| 108"L x 36"W x 36"H | Yes | 36.0" | 108.0" | 36.0" | Tuscana Rectangular Planter | Rectangular Planter |
| 108"L x 36"W x 42"H | Yes | 42.0" | 108.0" | 36.0" | Tuscana Rectangular Planter | Rectangular Planter |
| 108"L x 36"W x 48"H | Yes | 48.0" | 108.0" | 36.0" | Tuscana Rectangular Planter | Rectangular Planter |
| 108"L x 42"W x 18"H | Yes | 18.0" | 108.0" | 42.0" | Tuscana Rectangular Planter | Rectangular Planter |
| 108"L x 42"W x 24"H | Yes | 24.0" | 108.0" | 42.0" | Tuscana Rectangular Planter | Rectangular Planter |
| 108"L x 42"W x 30"H | Yes | 30.0" | 108.0" | 42.0" | Tuscana Rectangular Planter | Rectangular Planter |
| 108"L x 42"W x 36"H | Yes | 36.0" | 108.0" | 42.0" | Tuscana Rectangular Planter | Rectangular Planter |
| 108"L x 42"W x 42"H | Yes | 42.0" | 108.0" | 42.0" | Tuscana Rectangular Planter | Rectangular Planter |
| 108"L x 42"W x 48"H | Yes | 48.0" | 108.0" | 42.0" | Tuscana Rectangular Planter | Rectangular Planter |
| 120"L x 18"W x 18"H | Yes | 18.0" | 120.0" | 18.0" | Tuscana Rectangular Planter | Rectangular Planter |
| 120"L x 18"W x 24"H | Yes | 24.0" | 120.0" | 18.0" | Tuscana Rectangular Planter | Rectangular Planter |
| 120"L x 18"W x 30"H | Yes | 30.0" | 120.0" | 18.0" | Tuscana Rectangular Planter | Rectangular Planter |
| 120"L x 18"W x 36"H | Yes | 36.0" | 120.0" | 18.0" | Tuscana Rectangular Planter | Rectangular Planter |
| 120"L x 18"W x 42"H | Yes | 42.0" | 120.0" | 18.0" | Tuscana Rectangular Planter | Rectangular Planter |
| 120"L x 18"W x 48"H | Yes | 48.0" | 120.0" | 18.0" | Tuscana Rectangular Planter | Rectangular Planter |
| 120"L x 24"W x 18"H | Yes | 18.0" | 120.0" | 24.0" | Tuscana Rectangular Planter | Rectangular Planter |
| 120"L x 24"W x 24"H | Yes | 24.0" | 120.0" | 24.0" | Tuscana Rectangular Planter | Rectangular Planter |
| 120"L x 24"W x 30"H | Yes | 30.0" | 120.0" | 24.0" | Tuscana Rectangular Planter | Rectangular Planter |
| 120"L x 24"W x 36"H | Yes | 36.0" | 120.0" | 24.0" | Tuscana Rectangular Planter | Rectangular Planter |
| 120"L x 24"W x 42"H | Yes | 42.0" | 120.0" | 24.0" | Tuscana Rectangular Planter | Rectangular Planter |
| 120"L x 24"W x 48"H | Yes | 48.0" | 120.0" | 24.0" | Tuscana Rectangular Planter | Rectangular Planter |
| 120"L x 30"W x 18"H | Yes | 18.0" | 120.0" | 30.0" | Tuscana Rectangular Planter | Rectangular Planter |
| 120"L x 30"W x 24"H | Yes | 24.0" | 120.0" | 30.0" | Tuscana Rectangular Planter | Rectangular Planter |
| 120"L x 30"W x 30"H | Yes | 30.0" | 120.0" | 30.0" | Tuscana Rectangular Planter | Rectangular Planter |
| 120"L x 30"W x 36"H | Yes | 36.0" | 120.0" | 30.0" | Tuscana Rectangular Planter | Rectangular Planter |
| 120"L x 30"W x 42"H | Yes | 42.0" | 120.0" | 30.0" | Tuscana Rectangular Planter | Rectangular Planter |
| 120"L x 30"W x 48"H | Yes | 48.0" | 120.0" | 30.0" | Tuscana Rectangular Planter | Rectangular Planter |
| 120"L x 36"W x 18"H | Yes | 18.0" | 120.0" | 36.0" | Tuscana Rectangular Planter | Rectangular Planter |
| 120"L x 36"W x 24"H | Yes | 24.0" | 120.0" | 36.0" | Tuscana Rectangular Planter | Rectangular Planter |
| 120"L x 36"W x 30"H | Yes | 30.0" | 120.0" | 36.0" | Tuscana Rectangular Planter | Rectangular Planter |
| 120"L x 36"W x 36"H | Yes | 36.0" | 120.0" | 36.0" | Tuscana Rectangular Planter | Rectangular Planter |
| 120"L x 36"W x 42"H | Yes | 42.0" | 120.0" | 36.0" | Tuscana Rectangular Planter | Rectangular Planter |
| 120"L x 36"W x 48"H | Yes | 48.0" | 120.0" | 36.0" | Tuscana Rectangular Planter | Rectangular Planter |
| 120"L x 42"W x 18"H | Yes | 18.0" | 120.0" | 42.0" | Tuscana Rectangular Planter | Rectangular Planter |
| 120"L x 42"W x 24"H | Yes | 24.0" | 120.0" | 42.0" | Tuscana Rectangular Planter | Rectangular Planter |
| 120"L x 42"W x 30"H | Yes | 30.0" | 120.0" | 42.0" | Tuscana Rectangular Planter | Rectangular Planter |
| 120"L x 42"W x 36"H | Yes | 36.0" | 120.0" | 42.0" | Tuscana Rectangular Planter | Rectangular Planter |
| 120"L x 42"W x 42"H | Yes | 42.0" | 120.0" | 42.0" | Tuscana Rectangular Planter | Rectangular Planter |
| 120"L x 42"W x 48"H | Yes | 48.0" | 120.0" | 42.0" | Tuscana Rectangular Planter | Rectangular Planter |

## geometry (parser evidence)
native form markers: Sweep x1
no freeform markers — native parametric forms only
